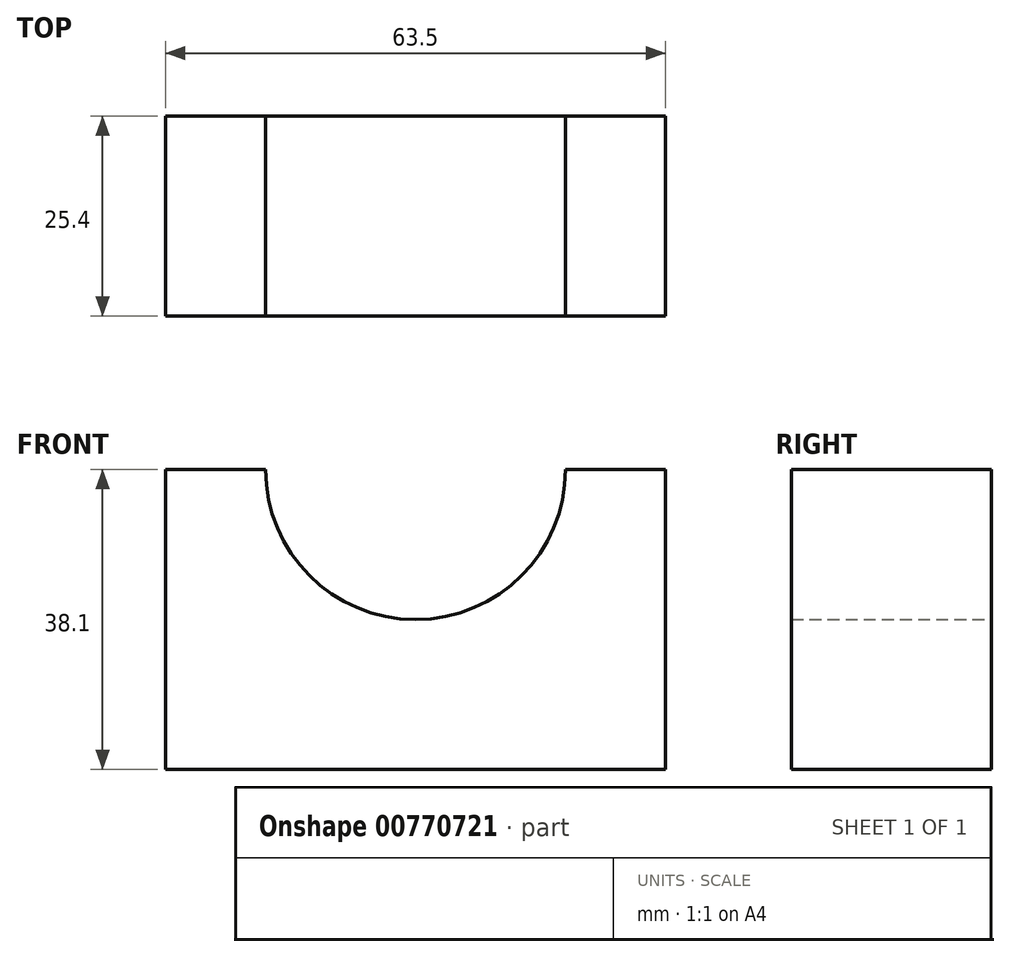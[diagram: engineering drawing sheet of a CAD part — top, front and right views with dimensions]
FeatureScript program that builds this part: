
annotation { "Feature Type Name" : "Feature", "Feature Type Description" : "" }
export const myFeature = defineFeature(function(context is Context, id is Id, definition is map)
    precondition{}
    {
        {
            var Q0;
            Q0=qCreatedBy(makeId("Right.planeOp"),FACE);
            var sketch = newSketch(context, id + "F0", { "sketchPlane" : qUnion([Q0])});
            skLineSegment(sketch, "E0.bottom", {"start": v(0, 0) * mm, "end": v(25.4, 0) * mm});
            skLineSegment(sketch, "E0.top", {"start": v(0, 38.1) * mm, "end": v(25.4, 38.1) * mm});
            skLineSegment(sketch, "E0.left", {"start": v(0, 0) * mm, "end": v(0, 38.1) * mm});
            skLineSegment(sketch, "E0.right", {"start": v(25.4, 0) * mm, "end": v(25.4, 38.1) * mm});
            skSolve(sketch);
        }
        {
            var Q0;
            Q0=qSketchRegion(id+"F0",true);
            extrude(context, id + "F1", {"entities" : qUnion([Q0]), "depth" : 63.5 * mm});
        }
        {
            var Q0;
            Q0=makeQuery(id+"F1.opExtrude","SWEPT_FACE",FACE,{"disambiguationData":[OSD([sQuery(id+"F0.wireOp",EDGE,"E0.right")])]});
            var sketch = newSketch(context, id + "F2", { "sketchPlane" : qUnion([Q0])});
            skCircle(sketch, "E1", {"center": v(-31.75, 38.1) * mm, "radius": 19.05 * mm});
            skSolve(sketch);
        }
        {
            var Q0;
            Q0=qSketchRegion(id+"F2",true);
            extrude(context, id + "F3", {"entities" : qUnion([Q0]), "operationType" : NewBodyOperationType.REMOVE, "oppositeDirection" : true, "depth" : 25.4 * mm});
        }
    });
